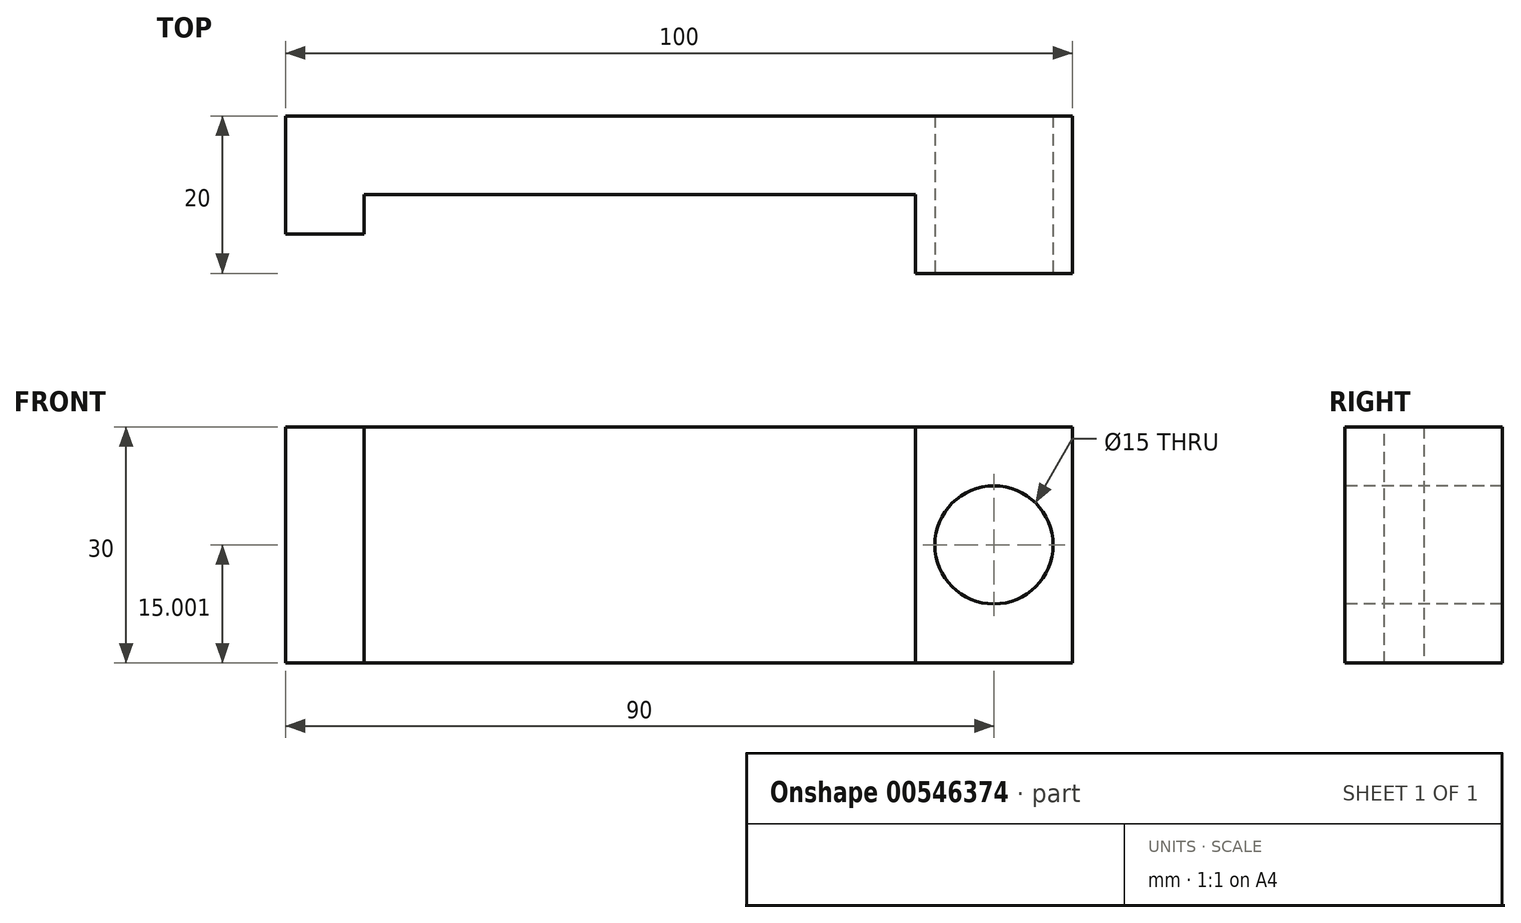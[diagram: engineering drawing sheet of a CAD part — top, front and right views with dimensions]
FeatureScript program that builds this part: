
annotation { "Feature Type Name" : "Feature", "Feature Type Description" : "" }
export const myFeature = defineFeature(function(context is Context, id is Id, definition is map)
    precondition{}
    {
        {
            var Q0;
            Q0=qCreatedBy(makeId("Front.planeOp"),FACE);
            var sketch = newSketch(context, id + "F0", { "sketchPlane" : qUnion([Q0])});
            skLineSegment(sketch, "E0.bottom", {"start": v(50, -15.89) * mm, "end": v(-50, -15.89) * mm});
            skLineSegment(sketch, "E0.top", {"start": v(50, 14.11) * mm, "end": v(-50, 14.11) * mm});
            skLineSegment(sketch, "E0.left", {"start": v(50, -15.89) * mm, "end": v(50, 14.11) * mm});
            skLineSegment(sketch, "E0.right", {"start": v(-50, -15.89) * mm, "end": v(-50, 14.11) * mm});
            skPoint(sketch, "E0.middle", {"position": v(0, -0.89) * mm});
            skSolve(sketch);
        }
        {
            var Q0;
            Q0 = qSketchRegion(id + "F0", true);
            extrude(context, id + "F1", {"entities" : qUnion([Q0]), "depth" : 10 * mm, "offsetDistance" : 25 * mm});
        }
        {
            var Q0;
            Q0=makeQuery(id+"F1.opExtrude","CAP_FACE",FACE,{"disambiguationData":[OSD([sQuery(id+"F0.wireOp",EDGE,"E0.bottom"),sQuery(id+"F0.wireOp",EDGE,"E0.top"),sQuery(id+"F0.wireOp",EDGE,"E0.left"),sQuery(id+"F0.wireOp",EDGE,"E0.right")])],"isStart":false});
            var sketch = newSketch(context, id + "F2", { "sketchPlane" : qUnion([Q0])});
            skLineSegment(sketch, "E1", {"start": v(-40, 14.11) * mm, "end": v(-40, -15.89) * mm});
            skSolve(sketch);
        }
        {
            var Q0;
            {var subQ0=sQuery(id+"F2.wireOp",EDGE,"E1");Q0=makeQuery(id+"F2.imprint","IMPRINT",FACE,{"disambiguationData":[TD([[makeQuery(id+"F2.imprint","IMPRINT",EDGE,{"derivedFrom":subQ0}),-1.0]])]});}
            extrude(context, id + "F3", {"entities" : qUnion([Q0]), "operationType" : NewBodyOperationType.ADD, "depth" : 5 * mm, "offsetDistance" : 25 * mm});
        }
        {
            var Q0;
            Q0=makeQuery(id+"F1.opExtrude","CAP_FACE",FACE,{"disambiguationData":[OSD([sQuery(id+"F0.wireOp",EDGE,"E0.bottom"),sQuery(id+"F0.wireOp",EDGE,"E0.top"),sQuery(id+"F0.wireOp",EDGE,"E0.left"),sQuery(id+"F0.wireOp",EDGE,"E0.right")])],"isStart":false});
            var sketch = newSketch(context, id + "F4", { "sketchPlane" : qUnion([Q0])});
            skLineSegment(sketch, "E2", {"start": v(30, 14.11) * mm, "end": v(30, -15.89) * mm});
            skSolve(sketch);
        }
        {
            var Q0;
            Q0 = qSketchRegion(id + "F4", true);
            var Q1;
            {var subQ0=sQuery(id+"F4.wireOp",EDGE,"E2");Q1=makeQuery(id+"F4.imprint","IMPRINT",FACE,{"disambiguationData":[TD([[makeQuery(id+"F4.imprint","IMPRINT",EDGE,{"derivedFrom":subQ0}),1.0]])]});}
            extrude(context, id + "F5", {"entities" : qUnion([Q0, Q1]), "operationType" : NewBodyOperationType.ADD, "depth" : 10 * mm, "offsetDistance" : 25 * mm});
        }
        {
            var Q0;
            Q0=makeQuery(id+"F5.opExtrude","CAP_FACE",FACE,{"disambiguationData":[OSD([sQuery(id+"F0.wireOp",EDGE,"E0.bottom"),sQuery(id+"F0.wireOp",EDGE,"E0.top"),sQuery(id+"F0.wireOp",EDGE,"E0.left"),sQuery(id+"F4.wireOp",EDGE,"E2")])],"isStart":false});
            var sketch = newSketch(context, id + "F6", { "sketchPlane" : qUnion([Q0])});
            skLineSegment(sketch, "E3", {"start": v(50, -15.89) * mm, "end": v(40, -15.89) * mm, "construction": true});
            skLineSegment(sketch, "E4", {"start": v(50, -15.89) * mm, "end": v(50, -0.89) * mm, "construction": true});
            skCircle(sketch, "E5", {"center": v(40, -0.89) * mm, "radius": 7.5 * mm});
            skSolve(sketch);
        }
        {
            var Q0;
            Q0=makeQuery(id+"F6.imprint","IMPRINT",FACE,{"disambiguationData":[TD([[makeQuery(id+"F6.imprint","IMPRINT",EDGE,{"derivedFrom":sQuery(id+"F6.wireOp",EDGE,"E5")}),1.0]])]});
            extrude(context, id + "F7", {"entities" : qUnion([Q0]), "operationType" : NewBodyOperationType.REMOVE, "endBound" : BoundingType.THROUGH_ALL, "oppositeDirection" : true, "depth" : 25 * mm, "offsetDistance" : 25 * mm});
        }
    });
